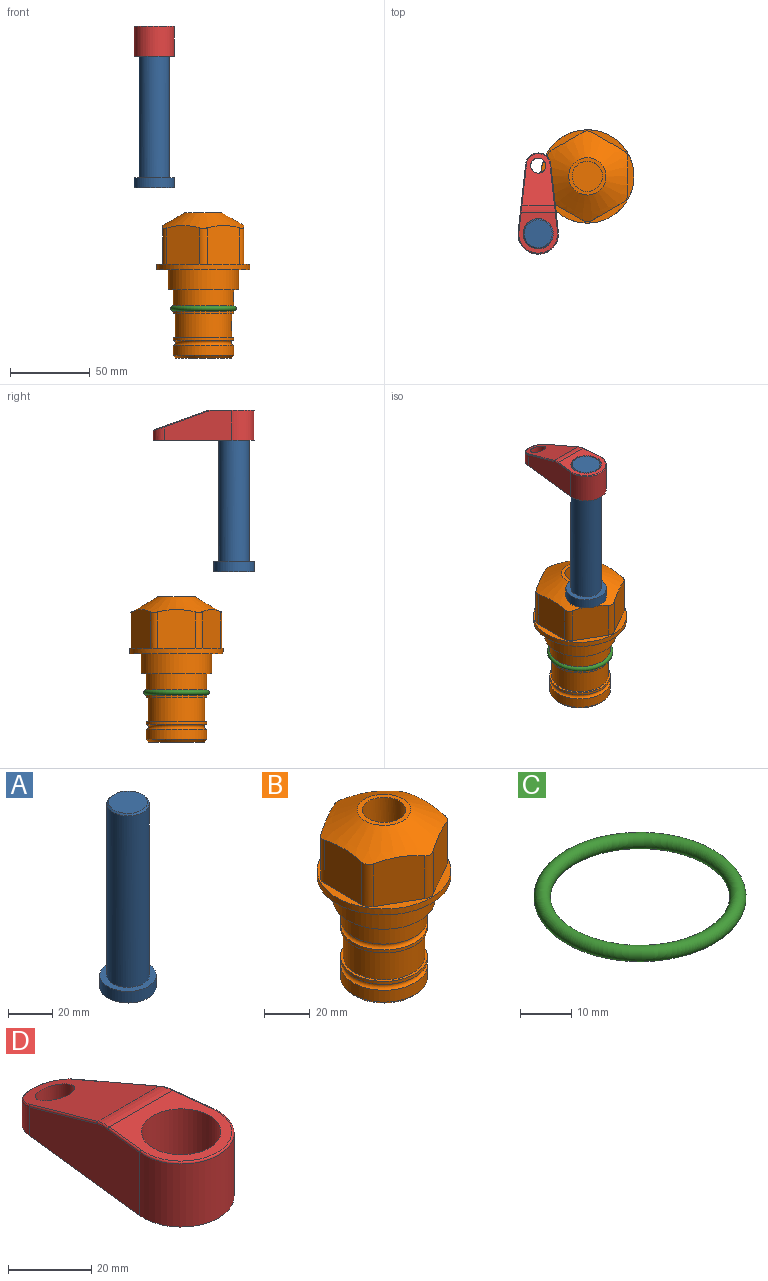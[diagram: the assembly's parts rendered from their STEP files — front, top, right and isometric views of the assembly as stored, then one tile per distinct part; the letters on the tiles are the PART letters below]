
ASSEMBLY  parts=4 mates=1
PART A: 6 faces, bbox 25.4x25.4x101.6 mm
  f0: plane 17.46x17.46mm, normal (0,0,1), area 239.5mm2, adj f5
  f1: plane 25.4x25.4mm, normal (0,0,-1), area 506.7mm2, adj f2
  f2: cylinder r=12.7mm len=25.4mm, axis (0,0,1), area 506.7mm2, adj f1,f3
  f3: plane 25.4x25.4mm, normal (0,0,1), area 221.7mm2, adj f2,f4
  f4: cylinder r=9.53mm len=94.46mm, axis (0,0,1), area 5653mm2, adj f3,f5
  f5: cone r=8.73mm half-angle=45deg, axis (0,0,-1), area 64.4mm2, adj f0,f4
PART B: 36 faces, bbox 58.7x58.7x91.2 mm
  f0: cylinder r=17.78mm len=35.56mm, axis (0,0,1), area 1670.8mm2, adj f23,f24,f31
  f1: cylinder r=19.05mm len=38.1mm, axis (0,0,1), area 1191.9mm2, adj f26,f27,f30
  f2: plane 58.66x58.66mm, normal (0,0,-1), area 1150.6mm2, adj f3,f28
  f3: cylinder r=29.33mm len=58.66mm, axis (0,0,-1), area 585.1mm2, adj f2,f4
  f4: plane 58.66x58.66mm, normal (0,0,1), area 475.9mm2, adj f3,f5,f6,f7,f8,f9,f10,f11
  f5: plane 24.5x20.32mm, normal (-0.5,0.87,0), area 562.8mm2, adj f4,f15,f16,f17
  f6: plane 24.5x20.32mm, normal (0.5,0.87,0), area 562.8mm2, adj f4,f14,f15,f17
  f7: plane 24.5x23.48mm, normal (1,0,0), area 562.8mm2, adj f4,f13,f14,f17
  f8: plane 24.5x20.32mm, normal (0.5,-0.87,0), area 562.8mm2, adj f4,f12,f13,f17
  f9: plane 24.5x20.32mm, normal (-0.5,-0.87,0), area 562.8mm2, adj f4,f11,f12,f17
  f10: plane 24.5x23.48mm, normal (-1,0,0), area 562.8mm2, adj f4,f11,f16,f17
  f11: cylinder r=5.08mm len=23.01mm, axis (0,0,-1), area 121.2mm2, adj f4,f9,f10,f17
  f12: cylinder r=5.08mm len=23.01mm, axis (0,0,-1), area 121.2mm2, adj f4,f8,f9,f17
  f13: cylinder r=5.08mm len=23.01mm, axis (0,0,-1), area 121.2mm2, adj f4,f7,f8,f17
  f14: cylinder r=5.08mm len=23.01mm, axis (0,0,-1), area 121.2mm2, adj f4,f6,f7,f17
  f15: cylinder r=5.08mm len=23.01mm, axis (0,0,-1), area 121.2mm2, adj f4,f5,f6,f17
  f16: cylinder r=5.08mm len=23.01mm, axis (0,0,-1), area 121.2mm2, adj f4,f5,f10,f17
  f17: cone r=11.73mm half-angle=60deg, axis (0,0,-1), area 2071.8mm2, adj f5,f6,f7,f8,f9,f10,f11,f12
  f18: plane 23.46x23.46mm, normal (0,0,1), area 147.4mm2, adj f17,f35
  f19: plane 34.93x34.93mm, normal (0,0,-1), area 958mm2, adj f29
  f20: cylinder r=19.05mm len=38.1mm, axis (0,0,1), area 760.1mm2, adj f21,f29
  f21: torus R=19.05mm, axis (0,0,1), area 565.3mm2, adj f20,f22
  f22: cylinder r=19.05mm len=38.1mm, axis (0,0,1), area 190mm2, adj f21,f23
  f23: plane 38.1x38.1mm, normal (0,0,1), area 146.9mm2, adj f0,f22
  f24: plane 38.1x38.1mm, normal (0,0,-1), area 146.9mm2, adj f0,f25
  f25: cylinder r=19.05mm len=38.1mm, axis (0,0,1), area 190mm2, adj f24,f26
  f26: torus R=19.05mm, axis (0,0,1), area 565.3mm2, adj f1,f25
  f27: plane 44.45x44.45mm, normal (0,0,-1), area 411.7mm2, adj f1,f28
  f28: cylinder r=22.23mm len=44.45mm, axis (0,0,1), area 1773.5mm2, adj f2,f27
  f29: cone r=19.05mm half-angle=45deg, axis (0,0,1), area 257.5mm2, adj f19,f20
  f30: cylinder r=3.17mm len=6.75mm, axis (-1,0,0), area 128mm2, adj f1,f33
  f31: cylinder r=3.17mm len=6.35mm, axis (-1,0,0), area 102.5mm2, adj f0,f33
  f32: plane 25.4x25.4mm, normal (0,0,1), area 506.7mm2, adj f33
  f33: cylinder r=12.7mm len=66.42mm, axis (0,0,-1), area 5236.2mm2, adj f30,f31,f32,f34
  f34: cone r=9.53mm half-angle=30deg, axis (0,0,-1), area 443.4mm2, adj f33,f35
  f35: cylinder r=9.53mm len=19.05mm, axis (0,0,-1), area 849mm2, adj f18,f34
PART C: 1 faces, bbox 44.7x44.7x3.2 mm
  f0: torus R=19.05mm, axis (0,0,1), area 1193.9mm2
PART D: 44 faces, bbox 27.5x64.5x19.1 mm
  f0: plane 2.3x0.95mm, normal (0,0,-1), area 1mm2, adj f25,f30,f34
  f1: plane 63.5x25.4mm, normal (0,0,-1), area 561.7mm2, adj f2,f3,f4,f5,f6,f7,f19,f20
  f2: cylinder r=12.7mm len=25.4mm, axis (0,0,-1), area 792.2mm2, adj f1,f3,f5,f13
  f3: plane 42.33x18.54mm, normal (0.99,0.11,0), area 647mm2, adj f1,f2,f4,f11,f12,f14
  f4: cylinder r=7.94mm len=15.78mm, axis (0,0,-1), area 158.6mm2, adj f1,f3,f5,f16
  f5: plane 42.33x18.54mm, normal (-0.99,0.11,0), area 647mm2, adj f1,f2,f4,f15,f17,f18
  f6: cylinder r=9.53mm len=19.05mm, axis (0,0,-1), area 1140.1mm2, adj f1,f8
  f7: cylinder r=4.76mm len=10.98mm, axis (0,0,-1), area 276.1mm2, adj f1,f9
  f8: plane 25.83x24.38mm, normal (0,0,1), area 262.2mm2, adj f6,f10,f11,f13,f15
  f9: plane 32.49x20.55mm, normal (0,0.34,0.94), area 489.9mm2, adj f7,f10,f14,f16,f18
  f10: cylinder r=12.7mm len=21.49mm, axis (-1,0,0), area 93.2mm2, adj f8,f9,f12,f17
  f11: cylinder r=0.51mm len=12.34mm, axis (0.11,-0.99,0), area 9.9mm2, adj f3,f8,f12,f13
  f12: bspline ~7.62x1.64mm, area 3.5mm2, adj f3,f10,f11,f14
  f13: torus R=12.19mm, axis (0,0,1), area 33.6mm2, adj f2,f8,f11,f15
  f14: cylinder r=0.51mm len=26.01mm, axis (0.1,-0.93,0.34), area 21.6mm2, adj f3,f9,f12,f16
  f15: cylinder r=0.51mm len=12.34mm, axis (0.11,0.99,0), area 9.9mm2, adj f5,f8,f13,f17
  f16: bspline ~15.78x7.05mm, area 15.7mm2, adj f4,f9,f14,f18
  f17: bspline ~7.62x1.64mm, area 3.5mm2, adj f5,f10,f15,f18
  f18: cylinder r=0.51mm len=26.01mm, axis (0.1,0.93,-0.34), area 21.6mm2, adj f5,f9,f16,f17
  f19: plane 21.6x14.29mm, normal (-0.99,-0.11,0), area 242.6mm2, adj f1,f26,f28,f34,f36,f38
  f20: plane 21.6x14.29mm, normal (0.99,-0.11,0), area 242.6mm2, adj f1,f27,f29,f37,f39,f41
  f21: cylinder r=12.7mm len=14.29mm, axis (0,0,-1), area 173.2mm2, adj f1,f26,f27,f30,f31,f33
  f22: cylinder r=7.94mm len=7.63mm, axis (0,0,-1), area 53.8mm2, adj f1,f28,f29,f42
  f23: plane 2.3x0.95mm, normal (0,0,-1), area 1mm2, adj f25,f33,f37
  f24: plane 17.94x12.32mm, normal (0,-0.34,-0.94), area 191.2mm2, adj f25,f38,f41,f42
  f25: cylinder r=9.53mm len=12.93mm, axis (-1,0,0), area 37.5mm2, adj f0,f23,f24,f31,f36,f39
  f26: cylinder r=1.59mm len=14.29mm, axis (0,0,-1), area 49mm2, adj f1,f19,f21,f32
  f27: cylinder r=1.59mm len=14.29mm, axis (0,0,-1), area 49mm2, adj f1,f20,f21,f35
  f28: cylinder r=1.59mm len=7.28mm, axis (0,0,-1), area 22.1mm2, adj f1,f19,f22,f40
  f29: cylinder r=1.59mm len=7.28mm, axis (0,0,-1), area 22.1mm2, adj f1,f20,f22,f43
  f30: torus R=14.29mm, axis (0,0,1), area 5.8mm2, adj f0,f21,f31,f32
  f31: bspline ~11.06x2.73mm, area 20.8mm2, adj f21,f25,f30,f33
  f32: sphere r=1.59mm, area 5.4mm2, adj f26,f30,f34
  f33: torus R=14.29mm, axis (0,0,1), area 5.8mm2, adj f21,f23,f31,f35
  f34: cylinder r=1.59mm len=1.68mm, axis (-0.11,0.99,0), area 2.4mm2, adj f0,f19,f32,f36
  f35: sphere r=1.59mm, area 5.4mm2, adj f27,f33,f37
  f36: bspline ~5.82x2.33mm, area 7.7mm2, adj f19,f25,f34,f38
  f37: cylinder r=1.59mm len=1.68mm, axis (0.11,0.99,0), area 2.4mm2, adj f20,f23,f35,f39
  f38: cylinder r=1.59mm len=18.33mm, axis (0.1,-0.93,0.34), area 46.7mm2, adj f19,f24,f36,f40
  f39: bspline ~5.82x2.33mm, area 7.7mm2, adj f20,f25,f37,f41
  f40: sphere r=1.59mm, area 3.6mm2, adj f28,f38,f42
  f41: cylinder r=1.59mm len=18.33mm, axis (0.1,0.93,-0.34), area 46.7mm2, adj f20,f24,f39,f43
  f42: bspline ~8.31x1.84mm, area 15.3mm2, adj f22,f24,f40,f43
  f43: sphere r=1.59mm, area 3.6mm2, adj f29,f41,f42
PLACE A t=(-30.87,-36.28,79.39)mm
PLACE B at identity fixed
PLACE C at identity
PLACE D t=(-30.87,-36.28,134)mm
MATE fastened A.f2 <-> D.f2  axis (0,0,1) through (-30.87,-36.28,153.05)mm
